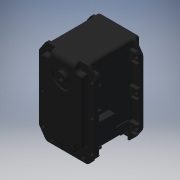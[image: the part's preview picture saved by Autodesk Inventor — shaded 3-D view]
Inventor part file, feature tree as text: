
AUTODESK INVENTOR PART (.ipt)
format: ipt  version: 2016 (Build 200138000, 138)  size: 714,752 bytes
history: native  units: in
note: dims shown in document units (in); Inventor stores cm internally (conversion verified against a paired STEP export)
features: other x3, sketch x3
ambient origin geometry x8: Origin, YZ Plane, XZ Plane, XY Plane, X Axis, Y Axis, Z Axis, Center Point
bodies: Solid1 (feature_tree)
feature tree (6):
  other  "MX-64T.ipt"
  other  "Solid1::MX-64T.ipt"
  other  "TaggingFeature1"
  sketch  "Sketch1"  dims[d0=0.3937in]
  sketch  "Sketch2"  dims[d2=0.1575in d3=0.0in d4=0.0in]
  sketch  "Sketch3"
